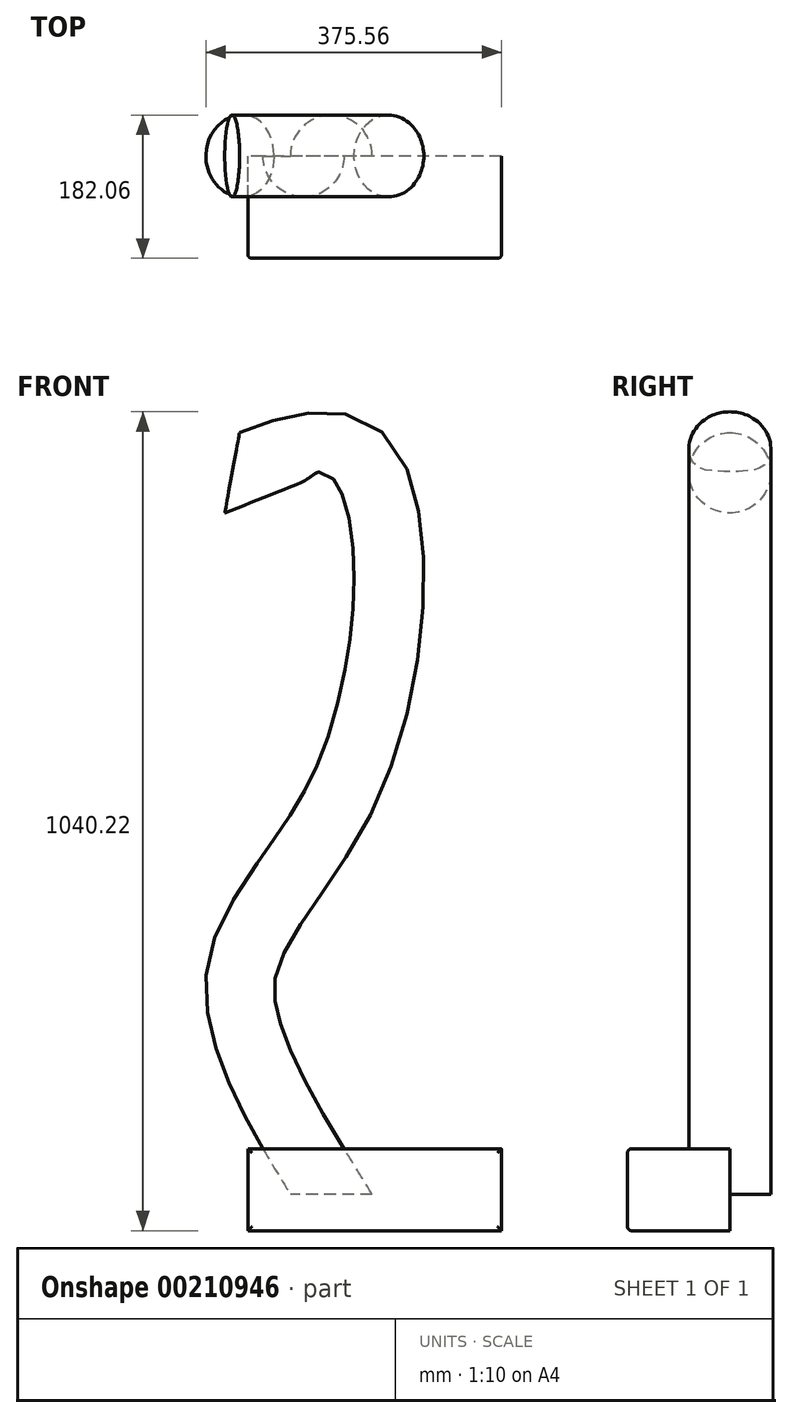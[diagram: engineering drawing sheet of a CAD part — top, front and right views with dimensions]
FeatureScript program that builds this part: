
annotation { "Feature Type Name" : "Feature", "Feature Type Description" : "" }
export const myFeature = defineFeature(function(context is Context, id is Id, definition is map)
    precondition{}
    {
        {
            var Q0;
            Q0=qCreatedBy(makeId("Front.planeOp"),FACE);
            var sketch = newSketch(context, id + "F0", { "sketchPlane" : qUnion([Q0])});
            skLineSegment(sketch, "E0.bottom", {"start": v(216.25, 57.5) * mm, "end": v(-105.84, 57.5) * mm});
            skLineSegment(sketch, "E0.top", {"start": v(216.25, -46.38) * mm, "end": v(-105.84, -46.38) * mm});
            skLineSegment(sketch, "E0.left", {"start": v(216.25, 57.5) * mm, "end": v(216.25, -46.38) * mm});
            skLineSegment(sketch, "E0.right", {"start": v(-105.84, 57.5) * mm, "end": v(-105.84, -46.38) * mm});
            skSolve(sketch);
        }
        {
            var Q0;
            Q0 = qSketchRegion(id + "F0", true);
            extrude(context, id + "F1", {"entities" : qUnion([Q0]), "depth" : 130.05 * mm});
        }
        {
            var Q0;
            Q0=makeQuery(id+"F1.opExtrude","CAP_FACE",FACE,{"disambiguationData":[OSD([sQuery(id+"F0.wireOp",EDGE,"E0.bottom"),sQuery(id+"F0.wireOp",EDGE,"E0.top"),sQuery(id+"F0.wireOp",EDGE,"E0.left"),sQuery(id+"F0.wireOp",EDGE,"E0.right")])],"isStart":false});
            fillet(context, id + "F2", {"entities" : qUnion([Q0]), "radius" : 5.08 * mm, "tangentPropagation" : true, "allowEdgeOverflow" : false});
        }
        {
            var Q0;
            Q0=makeQuery(id+"F1.opExtrude","SWEPT_FACE",FACE,{"disambiguationData":[OSD([sQuery(id+"F0.wireOp",EDGE,"E0.bottom")])]});
            var sketch = newSketch(context, id + "F3", { "sketchPlane" : qUnion([Q0])});
            skCircle(sketch, "E1", {"center": v(58.59, -81.59) * mm, "radius": 35.62 * mm});
            skSolve(sketch);
        }
        {
            var Q0;
            Q0=qCreatedBy(makeId("Top.planeOp"),FACE);
            var sketch = newSketch(context, id + "F4", { "sketchPlane" : qUnion([Q0])});
            skCircle(sketch, "E2", {"center": v(0, 0) * mm, "radius": 52.01 * mm});
            skSolve(sketch);
        }
        {
            var Q0;
            Q0=qCreatedBy(makeId("Front.planeOp"),FACE);
            var sketch = newSketch(context, id + "F5", { "sketchPlane" : qUnion([Q0])});
            skFitSpline(sketch, "E3", {"points": [v(0, 0) * mm, v(-112.23, 279.59) * mm, v(25.73, 537.18) * mm, v(36.02, 929.3) * mm, v(-125.93, 916.3) * mm], "startDerivative": vector(-711, 1148.21) * mm, "endDerivative": vector(-995.66, -387.73) * mm});
            skSolve(sketch);
        }
        {
            var Q0;
            Q0=makeQuery(id+"F4.imprint","IMPRINT",FACE,{"disambiguationData":[TD([[makeQuery(id+"F4.imprint","IMPRINT",EDGE,{"derivedFrom":sQuery(id+"F4.wireOp",EDGE,"E2")}),1.0]])]});
            var Q1;
            Q1=sQuery(id+"F5.wireOp",EDGE,"E3");
            sweep(context, id + "F6", {"operationType" : NewBodyOperationType.ADD, "profiles" : qUnion([Q0]), "path" : qUnion([Q1])});
        }
    });
